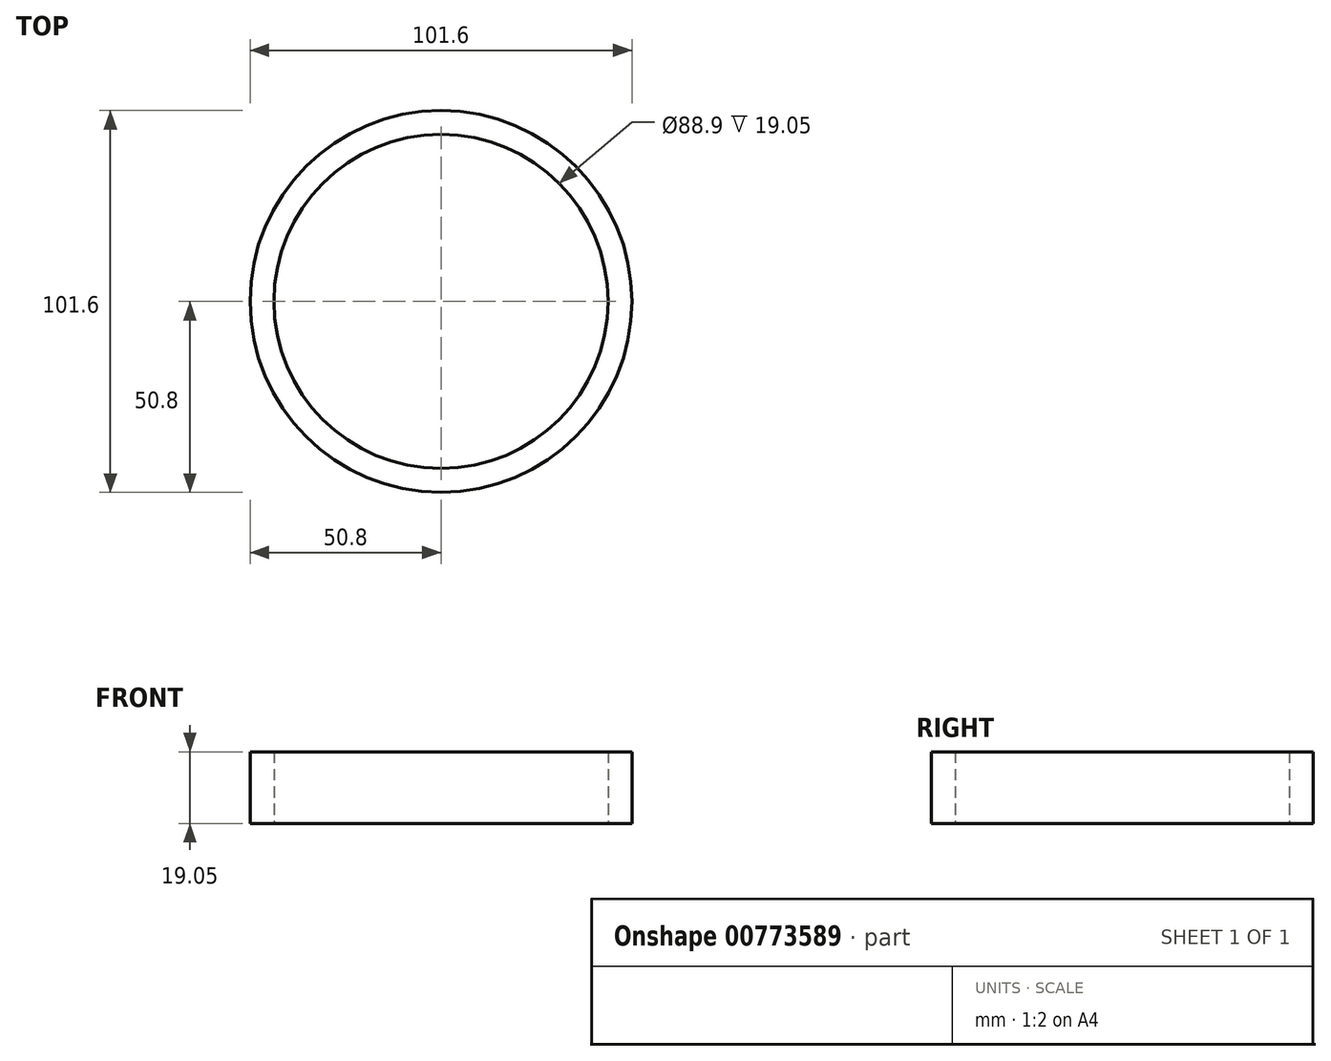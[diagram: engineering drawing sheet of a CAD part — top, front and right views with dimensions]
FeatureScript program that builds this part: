
annotation { "Feature Type Name" : "Feature", "Feature Type Description" : "" }
export const myFeature = defineFeature(function(context is Context, id is Id, definition is map)
    precondition{}
    {
        {
            var Q0;
            Q0=qCreatedBy(makeId("Top.planeOp"),FACE);
            var sketch = newSketch(context, id + "F0", { "sketchPlane" : qUnion([Q0])});
            skCircle(sketch, "E0", {"center": v(0, 0) * mm, "radius": 44.45 * mm});
            skCircle(sketch, "E1.0", {"center": v(0, 0) * mm, "radius": 50.8 * mm});
            skSolve(sketch);
        }
        {
            var Q0;
            Q0=makeQuery(id+"F0.imprint","IMPRINT",FACE,{"disambiguationData":[TD([[makeQuery(id+"F0.imprint","IMPRINT",EDGE,{"derivedFrom":sQuery(id+"F0.wireOp",EDGE,"E0")}),-1.0]])]});
            extrude(context, id + "F1", {"entities" : qUnion([Q0]), "depth" : 19.05 * mm, "offsetDistance" : 25.4 * mm});
        }
    });
